# Revit family: BOS-LineaSet-One_Familie
name_source: partatom
category: Türen
revit_build: Autodesk Revit 2017 (Build: 20160225_1515(x64)
units: mm (PartAtom-declared; Revit-internal decimal feet)

## family parameters
Basisbauteil = Wand
Beim Laden mit Abzugskörper schneiden = Nein
Gemeinsam genutzt = Nein
Immer vertikal = Ja
Raumberechnungspunkt = Ja

## types (4) — shared parameters
BE max. = 100 mm  [stored 0.328084 ft]
Bauelement = BOS Stahlzarge
Beschreibung = Schiebetürzarge LineaSet One, vormontiert, rahmenlos für in der Wand laufende Schiebetüren
Einfügepunkt = 25 mm  [stored 0.082021 ft]
Einlaufkastenprofil 1 = 187.9 mm
Funktion = Innen
Glastürblattstärke = 8 mm  [stored 0.0262467 ft]
Hersteller = BOS GmbH Best Of Steel, Lütkenfelde 4, D-48282 Emsdetten
Holztürblattstärke = 40 mm  [stored 0.131234 ft]
Info-Texte sichtbar = Ja
Information in English = Nein
MW max. = 150 mm  [stored 0.492126 ft]
MW min. = 125 mm  [stored 0.410105 ft]
Material = grundiert, feuerverzinktes Feinblech nach DIN EN 10143
Material - Anschraubprofil = <Nach Kategorie>
Material - Bürstendichtung = <Nach Kategorie>
Material - Führungszapfen = <Nach Kategorie>
Material - Laufschiene = <Nach Kategorie>
Material - Türgriff = <Nach Kategorie>
Material - Zarge = <Nach Kategorie>
Technische Infos rund um die Stahlzarge = www.BestOfSteel.de/tools-downloads/technische-infos-rund-um-die-stahlzarge/
Türblatteinstand hinten = 40 mm  [stored 0.131234 ft]
Türblatteinstand vorne = 9 mm  [stored 0.0295276 ft]
URL = www.BestOfSteel.de/stahlzargen/zargen-fuer-schiebetueren/lineaset-one/
Zargenblechstärke = 1.5 mm  [stored 0.00492126 ft]
zero-valued in all types: Breite, Dicke, Rohbaubreite, Rohbauhöhe

## per-type parameters (varying)
| type | ALU 100 BOS | ALU 80 BOS | Bürstendichtung | Glastürblatt | Holztürblatt | LineaSet One mit ALU 100 BOS Glas | LineaSet One mit ALU 100 BOS Holz | LineaSet One mit ALU 80 BOS Glas | LineaSet One mit ALU 80 BOS Holz | Material - Türblatt |
| LineaSet One mit ALU 80 BOS Holz | Nein | Ja | Nein | Nein | Ja | Nein | Nein | Nein | Ja | <Nach Kategorie> |
| LineaSet One mit ALU 100 BOS Holz | Ja | Nein | Nein | Nein | Ja | Nein | Ja | Nein | Nein | <Nach Kategorie> |
| LineaSet One mit ALU 100 BOS Glas | Ja | Nein | Ja | Ja | Nein | Ja | Nein | Nein | Nein | Glas |
| LineaSet One mit ALU 80 BOS Glas | Nein | Ja | Ja | Ja | Nein | Nein | Nein | Ja | Nein | Glas |

note: column(s) folded — value = type name in every type: Modell

note: [stored X ft] marks values corroborated as IEEE doubles in the binary element streams (Revit-internal decimal feet)
